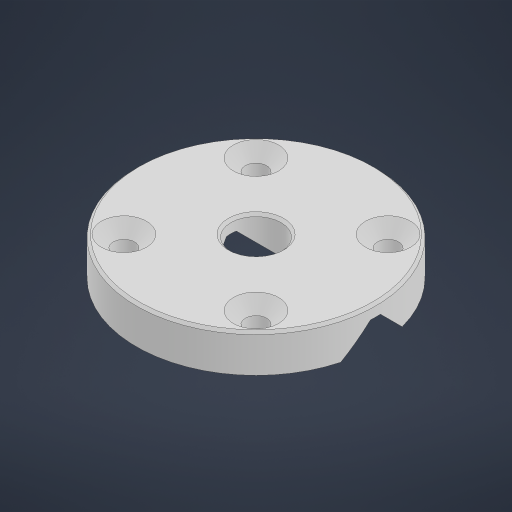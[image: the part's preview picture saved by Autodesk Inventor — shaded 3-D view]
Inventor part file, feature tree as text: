
AUTODESK INVENTOR PART (.ipt)
format: ipt  version: 2024.3 (Build 283343000, 343)  size: 239,616 bytes
history: native  units: mm
features: sketch x4, extrude x2, chamfer x2, hole x1, projected_geometry x1
ambient origin geometry x8: Origin, YZ Plane, XZ Plane, XY Plane, X Axis, Y Axis, Z Axis, Center Point
bodies: Solid1 (feature_tree)
feature tree (10):
  sketch  "Sketch1"  dims[d0=95.0mm d1=20.0mm]
  extrude  "Extrusion1"  Depth=20.0mm
  hole  "Hole1"  [1 undecoded]
  extrude  "Extrusion2"  TaperAngle=45.0deg  [1 undecoded]
  chamfer  "Chamfer1"  Distance=4.0mm
  chamfer  "Chamfer3"  [1 undecoded]
  sketch  "Sketch3"  dims[d5=8.5mm d6=18.0mm d7=18.0mm d8=2.0mm d9=90.0deg d10=20.4mm d11=20.594885mm d12=30.0mm]
  sketch  "Sketch4"  dims[d13=6.0mm d14=45.0deg d15=4.0mm d16=0.0mm d17=0.0mm d18=1.0mm d19=2.0mm d20=45.0deg d24=0.5mm d25=2.0mm d26=45.0deg d27=5.0mm d29=5.0mm d30=5.0mm d31=4.443651mm d32=5.0mm d33=52.5mm]
  sketch  "Sketch2"  dims[d3=15.0mm d4=0.0mm]
  projected_geometry  "Projected Loop1"
note: 3 required parameter values undecoded (feature->parameter linkage not recoverable at this tier; creation-order binding heuristic only, values carry confidence <= 0.55)
